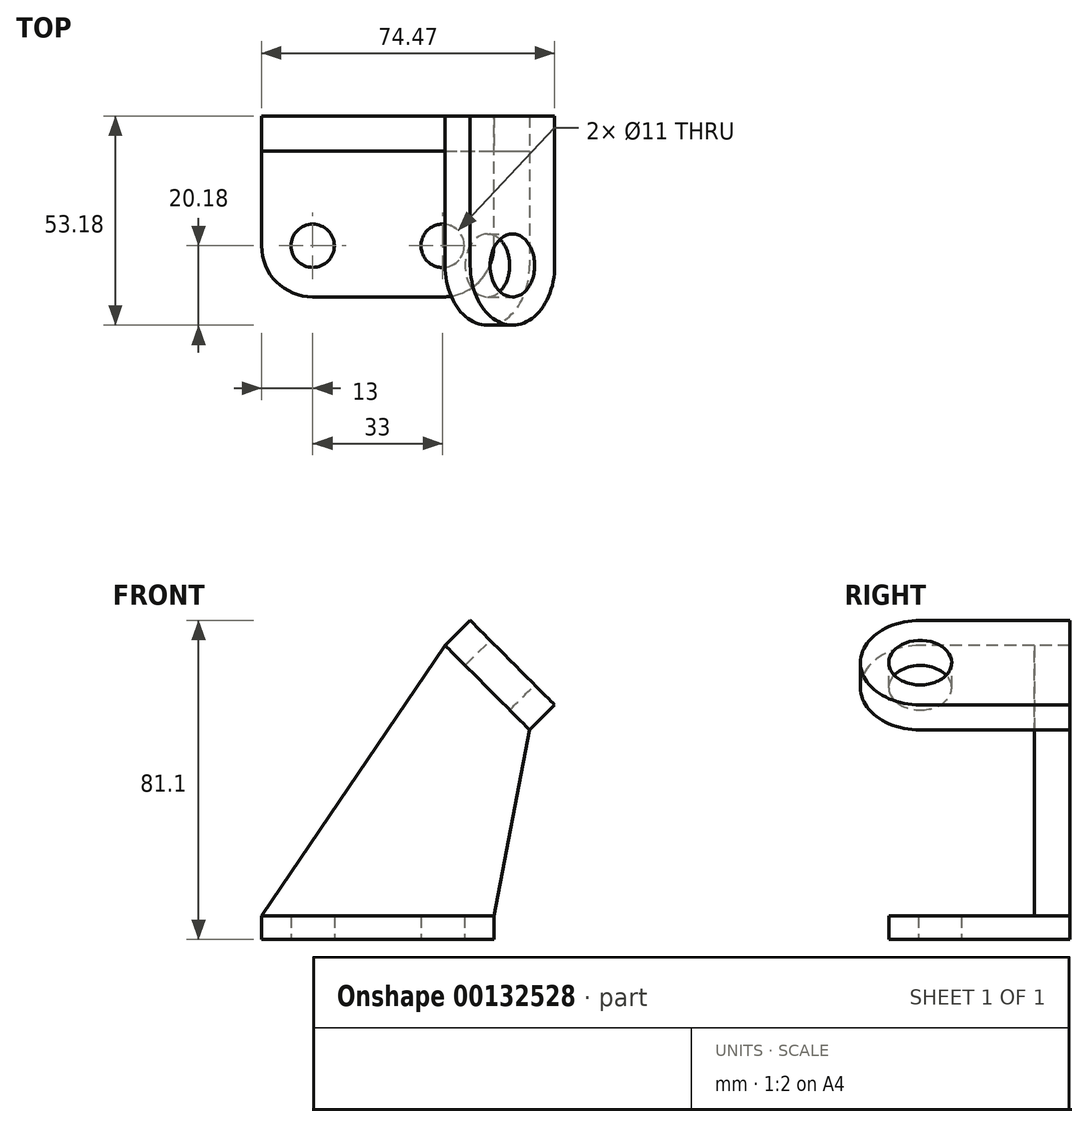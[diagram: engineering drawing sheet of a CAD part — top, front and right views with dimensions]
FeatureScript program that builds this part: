
annotation { "Feature Type Name" : "Feature", "Feature Type Description" : "" }
export const myFeature = defineFeature(function(context is Context, id is Id, definition is map)
    precondition{}
    {
        {
            var Q0;
            Q0=qCreatedBy(makeId("Top.planeOp"),FACE);
            var sketch = newSketch(context, id + "F0", { "sketchPlane" : qUnion([Q0])});
            skLineSegment(sketch, "E0", {"start": v(0, 37) * mm, "end": v(0, 13) * mm});
            skArc(sketch, "E1", {"start": v(0, 13) * mm, "mid": v(3.8, 3.8) * mm, "end": v(13, 0) * mm});
            skLineSegment(sketch, "E2", {"start": v(13, 0) * mm, "end": v(46, 0) * mm});
            skArc(sketch, "E3", {"start": v(46, 0) * mm, "mid": v(55.2, 3.8) * mm, "end": v(59, 13) * mm});
            skLineSegment(sketch, "E4", {"start": v(59, 13) * mm, "end": v(59, 37) * mm});
            skCircle(sketch, "E5", {"center": v(13, 13) * mm, "radius": 5.5 * mm});
            skCircle(sketch, "E6", {"center": v(46, 13) * mm, "radius": 5.5 * mm});
            skLineSegment(sketch, "E7", {"start": v(0, 37) * mm, "end": v(59, 37) * mm});
            skSolve(sketch);
        }
        {
            var Q0;
            Q0 = qSketchRegion(id + "F0", true);
            extrude(context, id + "F1", {"entities" : qUnion([Q0]), "depth" : 6 * mm});
        }
        {
            var Q0;
            Q0=makeQuery(id+"F1.opExtrude","SWEPT_FACE",FACE,{"disambiguationData":[OSD([sQuery(id+"F0.wireOp",EDGE,"E7")])]});
            var sketch = newSketch(context, id + "F2", { "sketchPlane" : qUnion([Q0])});
            skLineSegment(sketch, "E8", {"start": v(-59, 6) * mm, "end": v(-68.1, 53.27) * mm});
            skLineSegment(sketch, "E9", {"start": v(0, 6) * mm, "end": v(-46.64, 74.73) * mm});
            skLineSegment(sketch, "E10", {"start": v(-46.64, 74.73) * mm, "end": v(-68.1, 53.27) * mm});
            skLineSegment(sketch, "E11", {"start": v(-46.64, 74.73) * mm, "end": v(-114.8, 74.73) * mm, "construction": true});
            skPoint(sketch, "E12", {"position": v(-57.37, 64) * mm});
            skLineSegment(sketch, "E13", {"start": v(-59, 6) * mm, "end": v(-59, 0) * mm});
            skLineSegment(sketch, "E14", {"start": v(-59, 0) * mm, "end": v(0, 0) * mm});
            skLineSegment(sketch, "E15", {"start": v(0, 0) * mm, "end": v(0, 6) * mm});
            skSolve(sketch);
        }
        {
            var Q0;
            Q0 = qSketchRegion(id + "F2", true);
            extrude(context, id + "F3", {"entities" : qUnion([Q0]), "operationType" : NewBodyOperationType.ADD, "depth" : 9 * mm});
        }
        {
            var Q0;
            Q0=makeQuery(id+"F3.opExtrude","SWEPT_FACE",FACE,{"disambiguationData":[OSD([sQuery(id+"F2.wireOp",EDGE,"E10")])]});
            var sketch = newSketch(context, id + "F4", { "sketchPlane" : qUnion([Q0])});
            skLineSegment(sketch, "E16", {"start": v(37, 19.87) * mm, "end": v(8, 19.87) * mm});
            skLineSegment(sketch, "E17", {"start": v(37, -10.5) * mm, "end": v(8, -10.5) * mm});
            skArc(sketch, "E18", {"start": v(8, 19.87) * mm, "mid": v(-7.18, 4.69) * mm, "end": v(8, -10.5) * mm});
            skLineSegment(sketch, "E19", {"start": v(37, 19.87) * mm, "end": v(46, 19.87) * mm});
            skLineSegment(sketch, "E20", {"start": v(46, 19.87) * mm, "end": v(46, -10.5) * mm});
            skLineSegment(sketch, "E21", {"start": v(46, -10.5) * mm, "end": v(37, -10.5) * mm});
            skSolve(sketch);
        }
        {
            var Q0;
            Q0 = qSketchRegion(id + "F4", true);
            extrude(context, id + "F5", {"entities" : qUnion([Q0]), "operationType" : NewBodyOperationType.ADD, "depth" : 9 * mm});
        }
        {
            var Q0;
            Q0=makeQuery(id+"F5.opExtrude","CAP_FACE",FACE,{"disambiguationData":[OSD([sQuery(id+"F4.wireOp",EDGE,"E16"),sQuery(id+"F4.wireOp",EDGE,"E17"),sQuery(id+"F4.wireOp",EDGE,"E18"),sQuery(id+"F4.wireOp",EDGE,"E19"),sQuery(id+"F4.wireOp",EDGE,"E20"),sQuery(id+"F4.wireOp",EDGE,"E21")])],"isStart":false});
            var sketch = newSketch(context, id + "F6", { "sketchPlane" : qUnion([Q0])});
            skCircle(sketch, "E22", {"center": v(8, 4.69) * mm, "radius": 8 * mm});
            skSolve(sketch);
        }
        {
            var Q0;
            Q0 = qSketchRegion(id + "F6", true);
            extrude(context, id + "F7", {"entities" : qUnion([Q0]), "operationType" : NewBodyOperationType.REMOVE, "oppositeDirection" : true, "depth" : 9 * mm});
        }
    });
